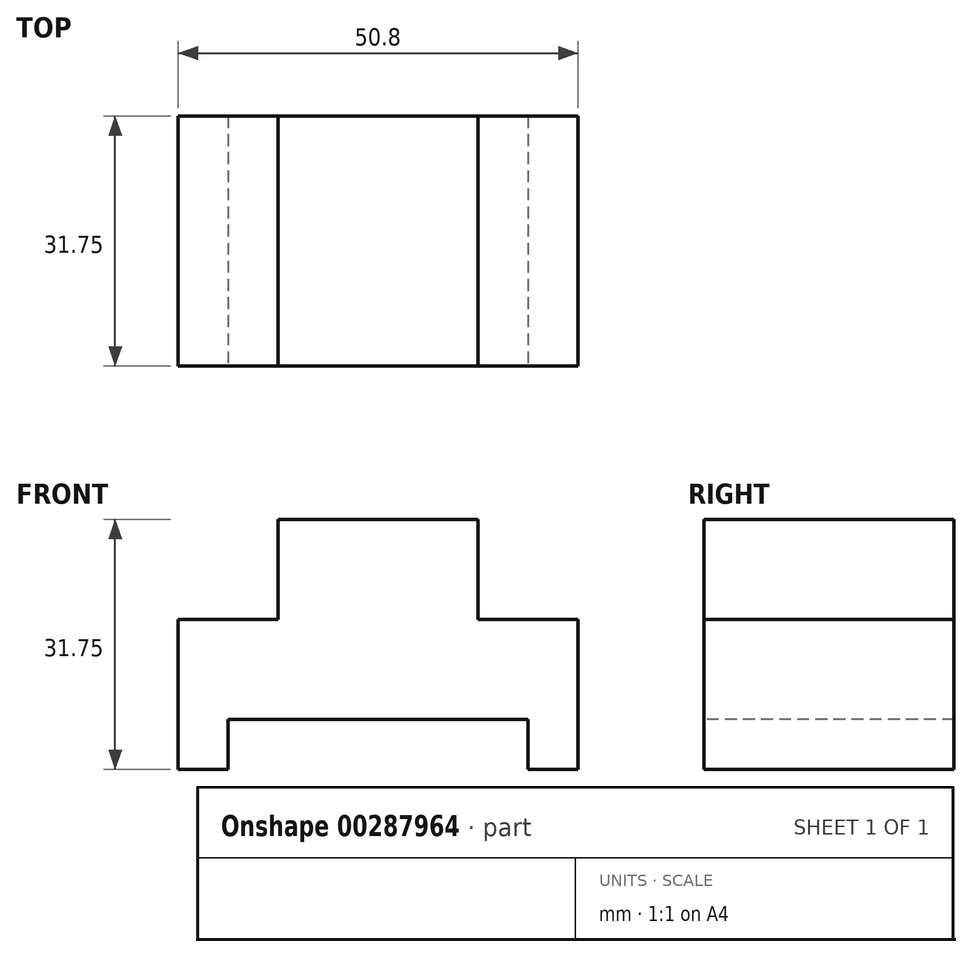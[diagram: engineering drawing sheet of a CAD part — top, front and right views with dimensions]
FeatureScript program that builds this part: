
annotation { "Feature Type Name" : "Feature", "Feature Type Description" : "" }
export const myFeature = defineFeature(function(context is Context, id is Id, definition is map)
    precondition{}
    {
        {
            var Q0;
            Q0=qCreatedBy(makeId("Front.planeOp"),FACE);
            var sketch = newSketch(context, id + "F0", { "sketchPlane" : qUnion([Q0])});
            skLineSegment(sketch, "E0.bottom", {"start": v(-26.98, 20.72) * mm, "end": v(23.82, 20.72) * mm});
            skLineSegment(sketch, "E0.top", {"start": v(-26.98, -11.03) * mm, "end": v(23.82, -11.03) * mm});
            skLineSegment(sketch, "E0.left", {"start": v(-26.98, 20.72) * mm, "end": v(-26.98, -11.03) * mm});
            skLineSegment(sketch, "E0.right", {"start": v(23.82, 20.72) * mm, "end": v(23.82, -11.03) * mm});
            skSolve(sketch);
        }
        {
            var Q0;
            Q0=makeQuery(id+"F0.imprint","IMPRINT",FACE,{"disambiguationData":[TD([[makeQuery(id+"F0.imprint","IMPRINT",EDGE,{"derivedFrom":sQuery(id+"F0.wireOp",EDGE,"E0.bottom")}),-1.0]])]});
            extrude(context, id + "F1", {"entities" : qUnion([Q0]), "depth" : 31.75 * mm});
        }
        {
            var Q0;
            Q0=makeQuery(id+"F1.opExtrude","CAP_FACE",FACE,{"disambiguationData":[OSD([sQuery(id+"F0.wireOp",EDGE,"E0.bottom"),sQuery(id+"F0.wireOp",EDGE,"E0.top"),sQuery(id+"F0.wireOp",EDGE,"E0.left"),sQuery(id+"F0.wireOp",EDGE,"E0.right")])],"isStart":false});
            var sketch = newSketch(context, id + "F2", { "sketchPlane" : qUnion([Q0])});
            skLineSegment(sketch, "E1.bottom", {"start": v(-20.63, -11.03) * mm, "end": v(17.47, -11.03) * mm});
            skLineSegment(sketch, "E1.top", {"start": v(-20.63, -4.68) * mm, "end": v(17.47, -4.68) * mm});
            skLineSegment(sketch, "E1.left", {"start": v(-20.63, -11.03) * mm, "end": v(-20.63, -4.68) * mm});
            skLineSegment(sketch, "E1.right", {"start": v(17.47, -11.03) * mm, "end": v(17.47, -4.68) * mm});
            skLineSegment(sketch, "E2.bottom", {"start": v(-26.98, 8.02) * mm, "end": v(-14.28, 8.02) * mm});
            skLineSegment(sketch, "E2.top", {"start": v(-26.98, 20.72) * mm, "end": v(-14.28, 20.72) * mm});
            skLineSegment(sketch, "E2.left", {"start": v(-26.98, 8.02) * mm, "end": v(-26.98, 20.72) * mm});
            skLineSegment(sketch, "E2.right", {"start": v(-14.28, 8.02) * mm, "end": v(-14.28, 20.72) * mm});
            skLineSegment(sketch, "E3.bottom", {"start": v(11.12, 20.72) * mm, "end": v(23.82, 20.72) * mm});
            skLineSegment(sketch, "E3.top", {"start": v(11.12, 8.02) * mm, "end": v(23.82, 8.02) * mm});
            skLineSegment(sketch, "E3.left", {"start": v(11.12, 20.72) * mm, "end": v(11.12, 8.02) * mm});
            skLineSegment(sketch, "E3.right", {"start": v(23.82, 20.72) * mm, "end": v(23.82, 8.02) * mm});
            skSolve(sketch);
        }
        {
            var Q0;
            Q0=makeQuery(id+"F2.imprint","IMPRINT",FACE,{"disambiguationData":[TD([[makeQuery(id+"F2.imprint","IMPRINT",EDGE,{"derivedFrom":sQuery(id+"F2.wireOp",EDGE,"E2.bottom")}),1.0]])]});
            var Q1;
            Q1=makeQuery(id+"F2.imprint","IMPRINT",FACE,{"disambiguationData":[TD([[makeQuery(id+"F2.imprint","IMPRINT",EDGE,{"derivedFrom":sQuery(id+"F2.wireOp",EDGE,"E3.bottom")}),-1.0]])]});
            var Q2;
            Q2=makeQuery(id+"F2.imprint","IMPRINT",FACE,{"disambiguationData":[TD([[makeQuery(id+"F2.imprint","IMPRINT",EDGE,{"derivedFrom":sQuery(id+"F2.wireOp",EDGE,"E1.bottom")}),1.0]])]});
            extrude(context, id + "F3", {"entities" : qUnion([Q0, Q1, Q2]), "operationType" : NewBodyOperationType.REMOVE, "oppositeDirection" : true, "depth" : 50.8 * mm});
        }
    });
